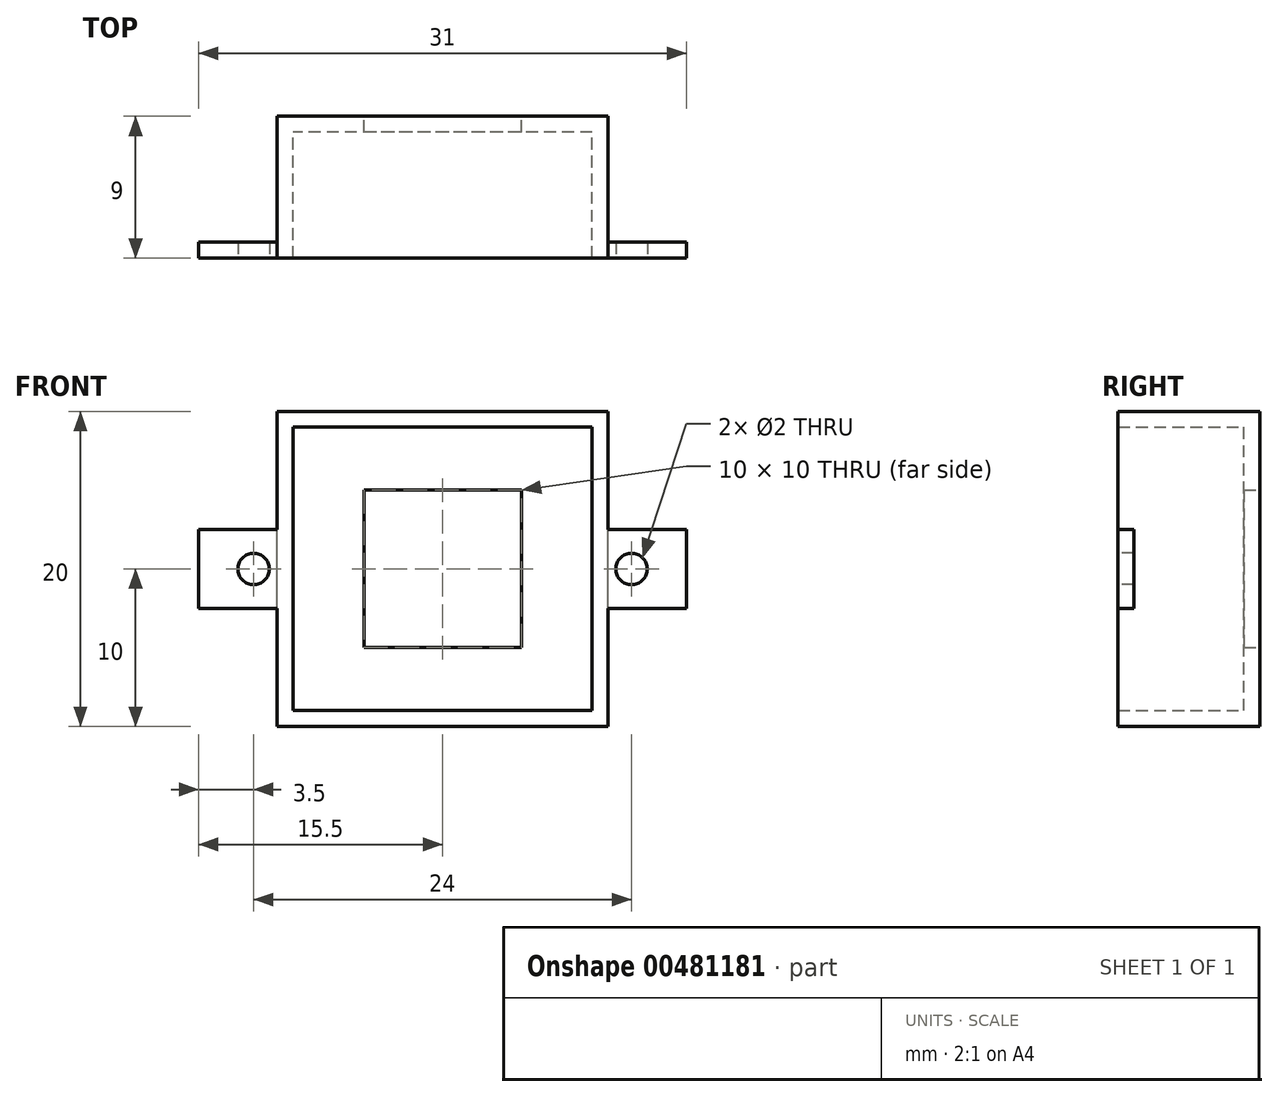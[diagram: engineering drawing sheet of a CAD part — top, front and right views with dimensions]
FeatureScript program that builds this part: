
annotation { "Feature Type Name" : "Feature", "Feature Type Description" : "" }
export const myFeature = defineFeature(function(context is Context, id is Id, definition is map)
    precondition{}
    {
        {
            var Q0;
            Q0=qCreatedBy(makeId("Front.planeOp"),FACE);
            var sketch = newSketch(context, id + "F0", { "sketchPlane" : qUnion([Q0])});
            skLineSegment(sketch, "E0.bottom", {"start": v(9, -8.5) * mm, "end": v(-9, -8.5) * mm});
            skLineSegment(sketch, "E0.top", {"start": v(9, 8.5) * mm, "end": v(-9, 8.5) * mm});
            skLineSegment(sketch, "E0.left", {"start": v(9, -8.5) * mm, "end": v(9, 8.5) * mm});
            skLineSegment(sketch, "E0.right", {"start": v(-9, -8.5) * mm, "end": v(-9, 8.5) * mm});
            skPoint(sketch, "E0.middle", {"position": v(0, 0) * mm});
            skLineSegment(sketch, "E1.bottom", {"start": v(9.5, -9) * mm, "end": v(-9.5, -9) * mm});
            skLineSegment(sketch, "E1.top", {"start": v(9.5, 9) * mm, "end": v(-9.5, 9) * mm});
            skLineSegment(sketch, "E1.left", {"start": v(9.5, -9) * mm, "end": v(9.5, 9) * mm});
            skLineSegment(sketch, "E1.right", {"start": v(-9.5, -9) * mm, "end": v(-9.5, 9) * mm});
            skLineSegment(sketch, "E2.bottom", {"start": v(10.5, -10) * mm, "end": v(-10.5, -10) * mm});
            skLineSegment(sketch, "E2.top", {"start": v(10.5, 10) * mm, "end": v(-10.5, 10) * mm});
            skLineSegment(sketch, "E2.left", {"start": v(10.5, -10) * mm, "end": v(10.5, 10) * mm});
            skLineSegment(sketch, "E2.right", {"start": v(-10.5, -10) * mm, "end": v(-10.5, 10) * mm});
            skLineSegment(sketch, "E3.bottom", {"start": v(5, 5) * mm, "end": v(-5, 5) * mm});
            skLineSegment(sketch, "E3.top", {"start": v(5, -5) * mm, "end": v(-5, -5) * mm});
            skLineSegment(sketch, "E3.left", {"start": v(5, 5) * mm, "end": v(5, -5) * mm});
            skLineSegment(sketch, "E3.right", {"start": v(-5, 5) * mm, "end": v(-5, -5) * mm});
            skSolve(sketch);
        }
        {
            var Q0;
            Q0=makeQuery(id+"F0.imprint","IMPRINT",FACE,{"disambiguationData":[TD([[makeQuery(id+"F0.imprint","IMPRINT",EDGE,{"derivedFrom":sQuery(id+"F0.wireOp",EDGE,"E0.bottom")}),-1.0]])]});
            var Q1;
            Q1=makeQuery(id+"F0.imprint","IMPRINT",FACE,{"disambiguationData":[TD([[makeQuery(id+"F0.imprint","IMPRINT",EDGE,{"derivedFrom":sQuery(id+"F0.wireOp",EDGE,"E0.bottom")}),1.0]])]});
            var Q2;
            Q2=makeQuery(id+"F0.imprint","IMPRINT",FACE,{"disambiguationData":[TD([[makeQuery(id+"F0.imprint","IMPRINT",EDGE,{"derivedFrom":sQuery(id+"F0.wireOp",EDGE,"E1.bottom")}),1.0]])]});
            extrude(context, id + "F1", {"entities" : qUnion([Q0, Q1, Q2]), "depth" : 1 * mm});
        }
        {
            var Q0;
            Q0=makeQuery(id+"F1.opExtrude","CAP_FACE",FACE,{"disambiguationData":[OSD([sQuery(id+"F0.wireOp",EDGE,"E2.bottom"),sQuery(id+"F0.wireOp",EDGE,"E2.top"),sQuery(id+"F0.wireOp",EDGE,"E2.left"),sQuery(id+"F0.wireOp",EDGE,"E2.right"),sQuery(id+"F0.wireOp",EDGE,"E3.bottom"),sQuery(id+"F0.wireOp",EDGE,"E3.top"),sQuery(id+"F0.wireOp",EDGE,"E3.left"),sQuery(id+"F0.wireOp",EDGE,"E3.right")])],"isStart":false});
            var sketch = newSketch(context, id + "F2", { "sketchPlane" : qUnion([Q0])});
            skLineSegment(sketch, "E4.bottom", {"start": v(10.5, -10) * mm, "end": v(-10.5, -10) * mm});
            skLineSegment(sketch, "E4.top", {"start": v(10.5, 10) * mm, "end": v(-10.5, 10) * mm});
            skLineSegment(sketch, "E4.left", {"start": v(10.5, -10) * mm, "end": v(10.5, 10) * mm});
            skLineSegment(sketch, "E4.right", {"start": v(-10.5, -10) * mm, "end": v(-10.5, 10) * mm});
            skPoint(sketch, "E4.middle", {"position": v(0, 0) * mm});
            skLineSegment(sketch, "E5.bottom", {"start": v(9.5, -9) * mm, "end": v(-9.5, -9) * mm});
            skLineSegment(sketch, "E5.top", {"start": v(9.5, 9) * mm, "end": v(-9.5, 9) * mm});
            skLineSegment(sketch, "E5.left", {"start": v(9.5, -9) * mm, "end": v(9.5, 9) * mm});
            skLineSegment(sketch, "E5.right", {"start": v(-9.5, -9) * mm, "end": v(-9.5, 9) * mm});
            skSolve(sketch);
        }
        {
            var Q0;
            Q0=makeQuery(id+"F2.imprint","IMPRINT",FACE,{"disambiguationData":[TD([[makeQuery(id+"F2.imprint","IMPRINT",EDGE,{"derivedFrom":sQuery(id+"F2.wireOp",EDGE,"E4.bottom")}),-1.0]])]});
            extrude(context, id + "F3", {"entities" : qUnion([Q0]), "operationType" : NewBodyOperationType.ADD, "depth" : 7 * mm});
        }
        {
            var Q0;
            Q0=makeQuery(id+"F3.opExtrude","CAP_FACE",FACE,{"disambiguationData":[OSD([sQuery(id+"F2.wireOp",EDGE,"E4.bottom"),sQuery(id+"F2.wireOp",EDGE,"E4.top"),sQuery(id+"F2.wireOp",EDGE,"E4.left"),sQuery(id+"F2.wireOp",EDGE,"E4.right"),sQuery(id+"F2.wireOp",EDGE,"E5.bottom"),sQuery(id+"F2.wireOp",EDGE,"E5.top"),sQuery(id+"F2.wireOp",EDGE,"E5.left"),sQuery(id+"F2.wireOp",EDGE,"E5.right")])],"isStart":false});
            var sketch = newSketch(context, id + "F4", { "sketchPlane" : qUnion([Q0])});
            skLineSegment(sketch, "E6.bottom", {"start": v(10.5, 10) * mm, "end": v(-10.5, 10) * mm});
            skLineSegment(sketch, "E6.top", {"start": v(10.5, -10) * mm, "end": v(-10.5, -10) * mm});
            skLineSegment(sketch, "E6.left", {"start": v(10.5, 10) * mm, "end": v(10.5, -10) * mm});
            skLineSegment(sketch, "E6.right", {"start": v(-10.5, 10) * mm, "end": v(-10.5, -10) * mm});
            skPoint(sketch, "E6.middle", {"position": v(0, 0) * mm});
            skLineSegment(sketch, "E7.bottom", {"start": v(9.5, 9) * mm, "end": v(-9.5, 9) * mm});
            skLineSegment(sketch, "E7.top", {"start": v(9.5, -9) * mm, "end": v(-9.5, -9) * mm});
            skLineSegment(sketch, "E7.left", {"start": v(9.5, 9) * mm, "end": v(9.5, -9) * mm});
            skLineSegment(sketch, "E7.right", {"start": v(-9.5, 9) * mm, "end": v(-9.5, -9) * mm});
            skPoint(sketch, "E8.middle", {"position": v(-10.5, 0) * mm});
            skPoint(sketch, "E9.middle", {"position": v(10.5, 0) * mm});
            skLineSegment(sketch, "E10.bottom", {"start": v(-10.5, -2.5) * mm, "end": v(-15.5, -2.5) * mm});
            skLineSegment(sketch, "E10.top", {"start": v(-10.5, 2.5) * mm, "end": v(-15.5, 2.5) * mm});
            skLineSegment(sketch, "E10.left", {"start": v(-10.5, -2.5) * mm, "end": v(-10.5, 2.5) * mm});
            skLineSegment(sketch, "E10.right", {"start": v(-15.5, -2.5) * mm, "end": v(-15.5, 2.5) * mm});
            skPoint(sketch, "E10.middle", {"position": v(-13, 0) * mm});
            skLineSegment(sketch, "E11.bottom", {"start": v(10.5, -2.5) * mm, "end": v(15.5, -2.5) * mm});
            skLineSegment(sketch, "E11.top", {"start": v(10.5, 2.5) * mm, "end": v(15.5, 2.5) * mm});
            skLineSegment(sketch, "E11.left", {"start": v(10.5, -2.5) * mm, "end": v(10.5, 2.5) * mm});
            skLineSegment(sketch, "E11.right", {"start": v(15.5, -2.5) * mm, "end": v(15.5, 2.5) * mm});
            skPoint(sketch, "E11.middle", {"position": v(13, 0) * mm});
            skSolve(sketch);
        }
        {
            var Q0;
            Q0=qSketchRegion(id+"F4",true);
            extrude(context, id + "F5", {"entities" : qUnion([Q0]), "operationType" : NewBodyOperationType.ADD, "depth" : 1 * mm});
        }
        {
            var Q0;
            Q0=makeQuery(id+"F5.opExtrude","CAP_FACE",FACE,{"disambiguationData":[OSD([sQuery(id+"F4.wireOp",EDGE,"E6.bottom"),sQuery(id+"F4.wireOp",EDGE,"E6.top"),sQuery(id+"F4.wireOp",EDGE,"E6.left"),sQuery(id+"F4.wireOp",EDGE,"E6.right"),sQuery(id+"F4.wireOp",EDGE,"E7.bottom"),sQuery(id+"F4.wireOp",EDGE,"E7.top"),sQuery(id+"F4.wireOp",EDGE,"E7.left"),sQuery(id+"F4.wireOp",EDGE,"E7.right"),sQuery(id+"F4.wireOp",EDGE,"E10.bottom"),sQuery(id+"F4.wireOp",EDGE,"E10.top"),sQuery(id+"F4.wireOp",EDGE,"E10.right"),sQuery(id+"F4.wireOp",EDGE,"E11.bottom"),sQuery(id+"F4.wireOp",EDGE,"E11.top"),sQuery(id+"F4.wireOp",EDGE,"E11.right")])],"isStart":false});
            var sketch = newSketch(context, id + "F6", { "sketchPlane" : qUnion([Q0])});
            skPoint(sketch, "E12", {"position": v(-12, 0) * mm});
            skPoint(sketch, "E13", {"position": v(12, 0) * mm});
            skSolve(sketch);
        }
        {
            var Q0;
            Q0=sQuery(id+"F6.wireOp",VERTEX,"E12");
            var Q1;
            Q1=sQuery(id+"F6.wireOp",VERTEX,"E13");
            var Q2;
            Q2=makeQuery(id+"F1.opExtrude","SWEPT_BODY",BODY,{"disambiguationData":[OSD([sQuery(id+"F0.wireOp",EDGE,"E2.bottom"),sQuery(id+"F0.wireOp",EDGE,"E2.top"),sQuery(id+"F0.wireOp",EDGE,"E2.left"),sQuery(id+"F0.wireOp",EDGE,"E2.right"),sQuery(id+"F0.wireOp",EDGE,"E3.bottom"),sQuery(id+"F0.wireOp",EDGE,"E3.top"),sQuery(id+"F0.wireOp",EDGE,"E3.left"),sQuery(id+"F0.wireOp",EDGE,"E3.right")])]});
            hole(context, id + "F7", {"style" : HoleStyle.SIMPLE, "endStyle" : HoleEndStyle.THROUGH, "holeDiameter" : 2 * mm, "isTappedThrough" : true, "tappedDepth" : 12 * mm, "tapClearance" : 3, "locations" : qUnion([Q0, Q1]), "scope" : qUnion([Q2])});
        }
    });
